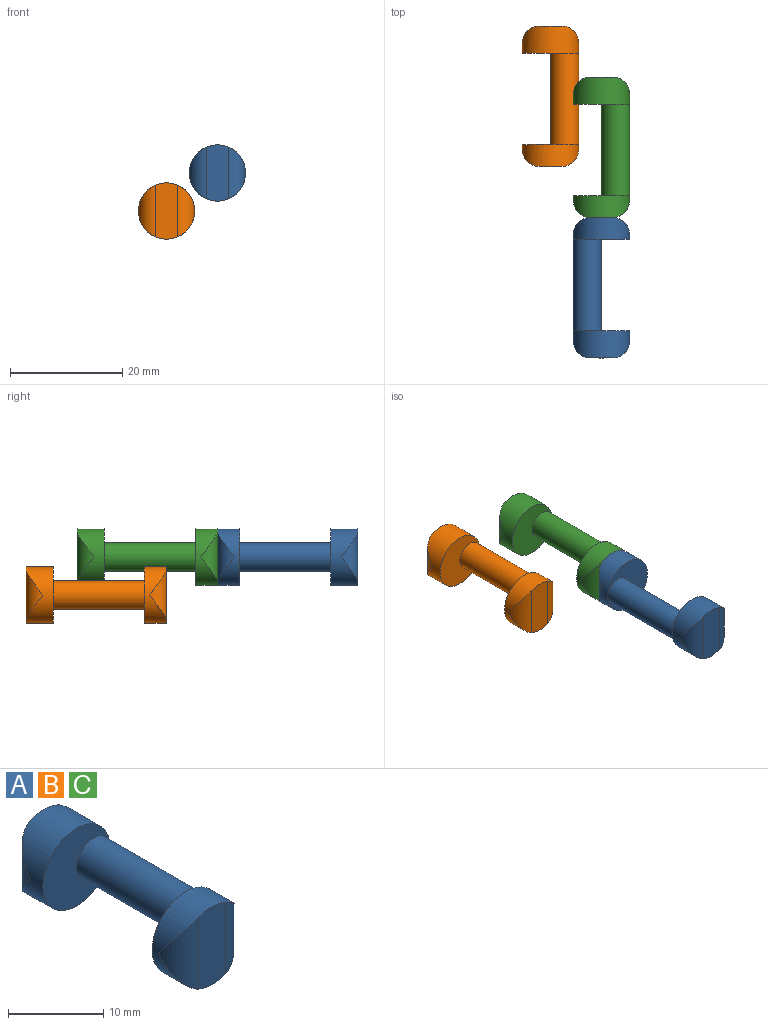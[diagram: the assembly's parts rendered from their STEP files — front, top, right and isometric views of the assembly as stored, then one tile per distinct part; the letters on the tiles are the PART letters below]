
ASSEMBLY  parts=3 mates=1
PART A: 11 faces, bbox 10x25x10 mm
  f0: cylinder r=5mm len=10mm, axis (0,1,0), area 126.5mm2, adj f1,f2,f3,f4
  f1: plane 10x4mm, normal (0,1,0), area 38.9mm2, adj f0,f2,f3
  f2: cylinder r=3mm len=9.17mm, axis (0,0,-1), area 24.9mm2, adj f0,f1
  f3: cylinder r=3mm len=9.17mm, axis (0,0,-1), area 24.9mm2, adj f0,f1
  f4: plane 10x10mm, normal (0,-1,0), area 58.9mm2, adj f0,f6
  f5: plane 10x10mm, normal (0,1,0), area 58.9mm2, adj f6,f10
  f6: cylinder r=2.5mm len=16.23mm, axis (0,1,0), area 255mm2, adj f4,f5
  f7: cylinder r=3mm len=9.17mm, axis (0,0,-1), area 24.9mm2, adj f8,f10
  f8: plane 10x4mm, normal (0,-1,0), area 38.9mm2, adj f7,f9,f10
  f9: cylinder r=3mm len=9.17mm, axis (0,0,-1), area 24.9mm2, adj f8,f10
  f10: cylinder r=5mm len=10mm, axis (0,1,0), area 96.6mm2, adj f5,f7,f8,f9
PART B: same geometry as A
PART C: same geometry as A
PLACE A rot(axis=(0,0,1),180deg) t=(-13.05,-59.1,6.77)mm
PLACE B t=(-22.12,0,0)mm
PLACE C t=(-13.05,-9.1,6.77)mm
MATE fastened A.f0 <-> C.f0  axis (0,1,0) through (-13.05,-34.1,6.77)mm
